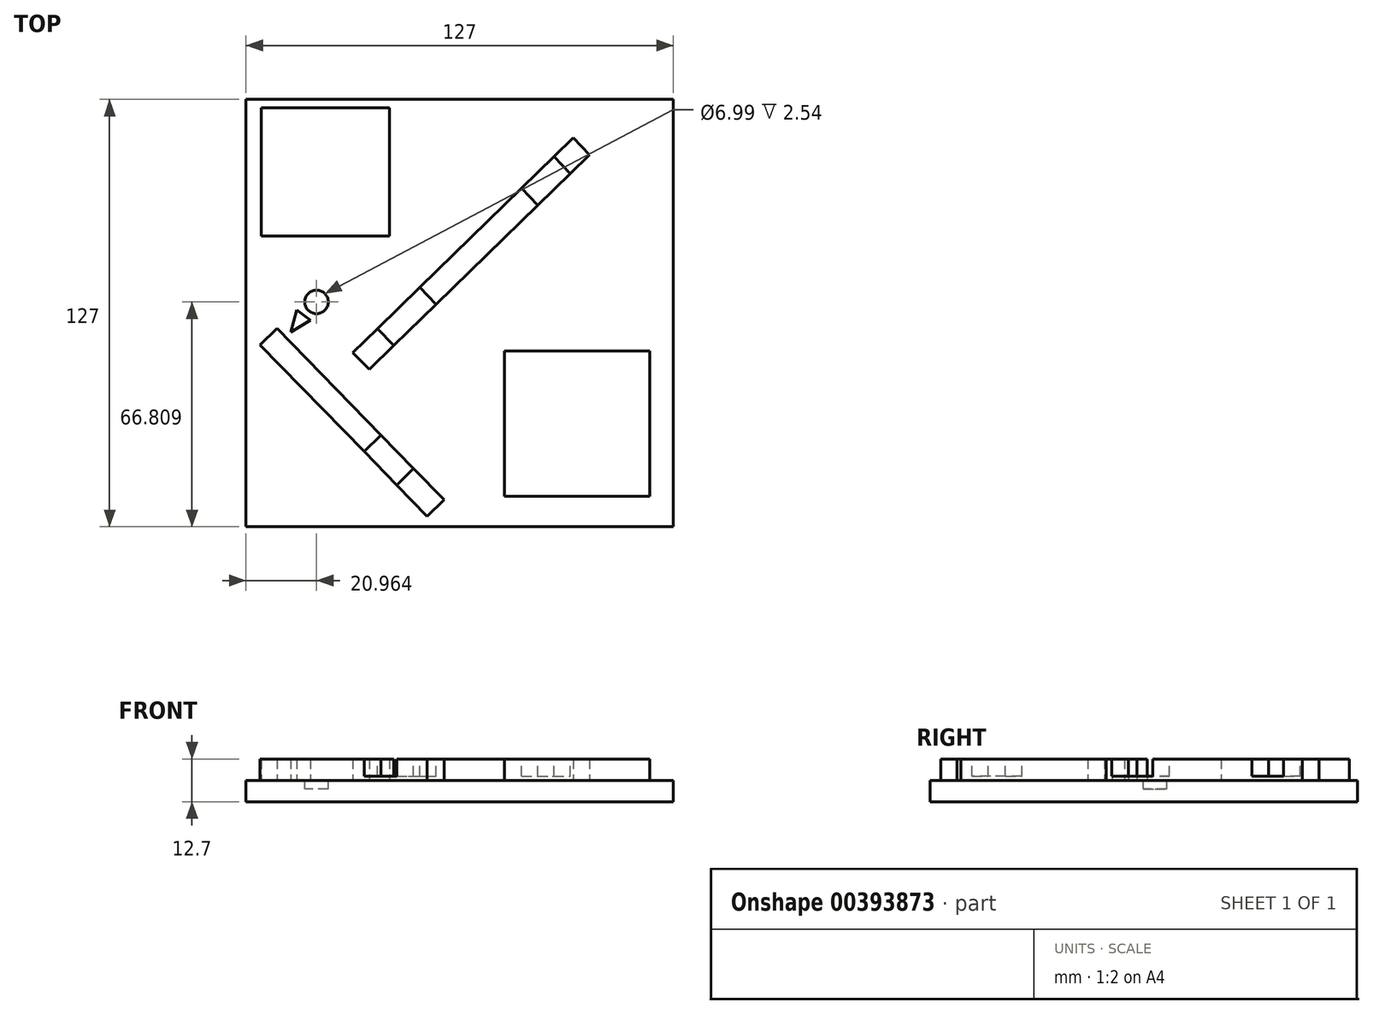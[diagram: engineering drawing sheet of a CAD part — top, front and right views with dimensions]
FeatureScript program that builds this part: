
annotation { "Feature Type Name" : "Feature", "Feature Type Description" : "" }
export const myFeature = defineFeature(function(context is Context, id is Id, definition is map)
    precondition{}
    {
        {
            var Q0;
            Q0=qCreatedBy(makeId("Top.planeOp"),FACE);
            var sketch = newSketch(context, id + "F0", { "sketchPlane" : qUnion([Q0])});
            skLineSegment(sketch, "E0.bottom", {"start": v(-62.96, 50.49) * mm, "end": v(64.04, 50.49) * mm});
            skLineSegment(sketch, "E0.top", {"start": v(-62.96, -76.51) * mm, "end": v(64.04, -76.51) * mm});
            skLineSegment(sketch, "E0.left", {"start": v(-62.96, 50.49) * mm, "end": v(-62.96, -76.51) * mm});
            skLineSegment(sketch, "E0.right", {"start": v(64.04, 50.49) * mm, "end": v(64.04, -76.51) * mm});
            skSolve(sketch);
        }
        {
            var Q0;
            Q0 = qSketchRegion(id + "F0", true);
            extrude(context, id + "F1", {"entities" : qUnion([Q0]), "depth" : 6.35 * mm});
        }
        {
            var Q0;
            Q0=makeQuery(id+"F1.opExtrude","CAP_FACE",FACE,{"disambiguationData":[OSD([sQuery(id+"F0.wireOp",EDGE,"E0.bottom"),sQuery(id+"F0.wireOp",EDGE,"E0.top"),sQuery(id+"F0.wireOp",EDGE,"E0.left"),sQuery(id+"F0.wireOp",EDGE,"E0.right")])],"isStart":false});
            var sketch = newSketch(context, id + "F2", { "sketchPlane" : qUnion([Q0])});
            skLineSegment(sketch, "E1", {"start": v(-58.74, -22.46) * mm, "end": v(-9.12, -73.4) * mm});
            skLineSegment(sketch, "E2", {"start": v(-9.12, -73.4) * mm, "end": v(-4.12, -68.53) * mm});
            skLineSegment(sketch, "E3", {"start": v(-58.74, -22.46) * mm, "end": v(-53.74, -17.59) * mm});
            skLineSegment(sketch, "E4", {"start": v(-53.74, -17.59) * mm, "end": v(-4.12, -68.53) * mm});
            skSolve(sketch);
        }
        {
            var Q0;
            Q0 = qSketchRegion(id + "F2", true);
            extrude(context, id + "F3", {"entities" : qUnion([Q0]), "operationType" : NewBodyOperationType.ADD, "depth" : 6.35 * mm});
        }
        {
            var Q0;
            Q0=makeQuery(id+"F3.opExtrude","CAP_FACE",FACE,{"disambiguationData":[OSD([sQuery(id+"F2.wireOp",EDGE,"E1"),sQuery(id+"F2.wireOp",EDGE,"E2"),sQuery(id+"F2.wireOp",EDGE,"E3"),sQuery(id+"F2.wireOp",EDGE,"E4")])],"isStart":false});
            var sketch = newSketch(context, id + "F4", { "sketchPlane" : qUnion([Q0])});
            skLineSegment(sketch, "E5", {"start": v(-27.84, -54.18) * mm, "end": v(-22.84, -49.31) * mm});
            skLineSegment(sketch, "E6", {"start": v(-18.16, -64.12) * mm, "end": v(-13.16, -59.25) * mm});
            skSolve(sketch);
        }
        {
            var Q0;
            {var subQ0=sQuery(id+"F4.wireOp",EDGE,"E5");Q0=makeQuery(id+"F4.imprint","IMPRINT",FACE,{"disambiguationData":[TD([[makeQuery(id+"F4.imprint","IMPRINT",EDGE,{"derivedFrom":subQ0}),-1.0]])]});}
            extrude(context, id + "F5", {"entities" : qUnion([Q0]), "operationType" : NewBodyOperationType.REMOVE, "oppositeDirection" : true, "depth" : 5.08 * mm});
        }
        {
            var Q0;
            Q0=makeQuery(id+"F1.opExtrude","CAP_FACE",FACE,{"disambiguationData":[OSD([sQuery(id+"F0.wireOp",EDGE,"E0.bottom"),sQuery(id+"F0.wireOp",EDGE,"E0.top"),sQuery(id+"F0.wireOp",EDGE,"E0.left"),sQuery(id+"F0.wireOp",EDGE,"E0.right")])],"isStart":false});
            var sketch = newSketch(context, id + "F6", { "sketchPlane" : qUnion([Q0])});
            skLineSegment(sketch, "E7.bottom", {"start": v(13.87, -24.28) * mm, "end": v(57.05, -24.28) * mm});
            skLineSegment(sketch, "E7.top", {"start": v(13.87, -67.46) * mm, "end": v(57.05, -67.46) * mm});
            skLineSegment(sketch, "E7.left", {"start": v(13.87, -24.28) * mm, "end": v(13.87, -67.46) * mm});
            skLineSegment(sketch, "E7.right", {"start": v(57.05, -24.28) * mm, "end": v(57.05, -67.46) * mm});
            skSolve(sketch);
        }
        {
            var Q0;
            Q0 = qSketchRegion(id + "F6", true);
            extrude(context, id + "F7", {"entities" : qUnion([Q0]), "operationType" : NewBodyOperationType.ADD, "depth" : 6.35 * mm});
        }
        {
            var Q0;
            Q0=makeQuery(id+"F1.opExtrude","CAP_FACE",FACE,{"disambiguationData":[OSD([sQuery(id+"F0.wireOp",EDGE,"E0.bottom"),sQuery(id+"F0.wireOp",EDGE,"E0.top"),sQuery(id+"F0.wireOp",EDGE,"E0.left"),sQuery(id+"F0.wireOp",EDGE,"E0.right")])],"isStart":false});
            var sketch = newSketch(context, id + "F8", { "sketchPlane" : qUnion([Q0])});
            skLineSegment(sketch, "E8", {"start": v(-31.22, -24.76) * mm, "end": v(-26.35, -29.77) * mm});
            skLineSegment(sketch, "E9", {"start": v(-31.22, -24.76) * mm, "end": v(34.29, 39.03) * mm});
            skLineSegment(sketch, "E10", {"start": v(34.29, 39.03) * mm, "end": v(39.16, 34.03) * mm});
            skLineSegment(sketch, "E11", {"start": v(-26.35, -29.77) * mm, "end": v(39.16, 34.03) * mm});
            skSolve(sketch);
        }
        {
            var Q0;
            Q0 = qSketchRegion(id + "F8", true);
            extrude(context, id + "F9", {"entities" : qUnion([Q0]), "operationType" : NewBodyOperationType.ADD, "depth" : 6.35 * mm});
        }
        {
            var Q0;
            Q0=makeQuery(id+"F9.opExtrude","CAP_FACE",FACE,{"disambiguationData":[OSD([sQuery(id+"F8.wireOp",EDGE,"E8"),sQuery(id+"F8.wireOp",EDGE,"E9"),sQuery(id+"F8.wireOp",EDGE,"E10"),sQuery(id+"F8.wireOp",EDGE,"E11")])],"isStart":false});
            var sketch = newSketch(context, id + "F10", { "sketchPlane" : qUnion([Q0])});
            skLineSegment(sketch, "E12", {"start": v(-23.88, -17.62) * mm, "end": v(-19, -22.62) * mm});
            skLineSegment(sketch, "E13", {"start": v(-11.34, -5.4) * mm, "end": v(-6.47, -10.41) * mm});
            skLineSegment(sketch, "E14", {"start": v(28.56, 33.46) * mm, "end": v(33.43, 28.45) * mm});
            skLineSegment(sketch, "E15", {"start": v(18.92, 24.07) * mm, "end": v(23.8, 19.07) * mm});
            skSolve(sketch);
        }
        {
            var Q0;
            {var subQ0=sQuery(id+"F10.wireOp",EDGE,"E12");Q0=makeQuery(id+"F10.imprint","IMPRINT",FACE,{"disambiguationData":[TD([[makeQuery(id+"F10.imprint","IMPRINT",EDGE,{"derivedFrom":subQ0}),1.0]])]});}
            var Q1;
            {var subQ0=sQuery(id+"F10.wireOp",EDGE,"E14");Q1=makeQuery(id+"F10.imprint","IMPRINT",FACE,{"disambiguationData":[TD([[makeQuery(id+"F10.imprint","IMPRINT",EDGE,{"derivedFrom":subQ0}),-1.0]])]});}
            extrude(context, id + "F11", {"entities" : qUnion([Q0, Q1]), "operationType" : NewBodyOperationType.REMOVE, "oppositeDirection" : true, "depth" : 5.08 * mm});
        }
        {
            var Q0;
            Q0=makeQuery(id+"F1.opExtrude","CAP_FACE",FACE,{"disambiguationData":[OSD([sQuery(id+"F0.wireOp",EDGE,"E0.bottom"),sQuery(id+"F0.wireOp",EDGE,"E0.top"),sQuery(id+"F0.wireOp",EDGE,"E0.left"),sQuery(id+"F0.wireOp",EDGE,"E0.right")])],"isStart":false});
            var sketch = newSketch(context, id + "F12", { "sketchPlane" : qUnion([Q0])});
            skLineSegment(sketch, "E16.bottom", {"start": v(-58.46, 47.95) * mm, "end": v(-20.36, 47.95) * mm});
            skLineSegment(sketch, "E16.top", {"start": v(-58.46, 9.85) * mm, "end": v(-20.36, 9.85) * mm});
            skLineSegment(sketch, "E16.left", {"start": v(-58.46, 47.95) * mm, "end": v(-58.46, 9.85) * mm});
            skLineSegment(sketch, "E16.right", {"start": v(-20.36, 47.95) * mm, "end": v(-20.36, 9.85) * mm});
            skSolve(sketch);
        }
        {
            var Q0;
            Q0 = qSketchRegion(id + "F12", true);
            extrude(context, id + "F13", {"entities" : qUnion([Q0]), "operationType" : NewBodyOperationType.ADD, "depth" : 6.35 * mm});
        }
        {
            var Q0;
            Q0=makeQuery(id+"F1.opExtrude","CAP_FACE",FACE,{"disambiguationData":[OSD([sQuery(id+"F0.wireOp",EDGE,"E0.bottom"),sQuery(id+"F0.wireOp",EDGE,"E0.top"),sQuery(id+"F0.wireOp",EDGE,"E0.left"),sQuery(id+"F0.wireOp",EDGE,"E0.right")])],"isStart":false});
            var sketch = newSketch(context, id + "F14", { "sketchPlane" : qUnion([Q0])});
            skCircle(sketch, "E17", {"center": v(-42, -9.7) * mm, "radius": 3.5 * mm});
            skSolve(sketch);
        }
        {
            var Q0;
            Q0 = qSketchRegion(id + "F14", true);
            extrude(context, id + "F15", {"entities" : qUnion([Q0]), "operationType" : NewBodyOperationType.REMOVE, "oppositeDirection" : true, "depth" : 2.54 * mm});
        }
        {
            var Q0;
            Q0=makeQuery(id+"F1.opExtrude","CAP_FACE",FACE,{"disambiguationData":[OSD([sQuery(id+"F0.wireOp",EDGE,"E0.bottom"),sQuery(id+"F0.wireOp",EDGE,"E0.top"),sQuery(id+"F0.wireOp",EDGE,"E0.left"),sQuery(id+"F0.wireOp",EDGE,"E0.right")])],"isStart":false});
            var sketch = newSketch(context, id + "F16", { "sketchPlane" : qUnion([Q0])});
            skLineSegment(sketch, "E18", {"start": v(-47.91, -12.1) * mm, "end": v(-49.66, -18.74) * mm});
            skLineSegment(sketch, "E19", {"start": v(-49.66, -18.74) * mm, "end": v(-43.83, -15.13) * mm});
            skLineSegment(sketch, "E20", {"start": v(-43.83, -15.13) * mm, "end": v(-47.91, -12.1) * mm});
            skSolve(sketch);
        }
        {
            var Q0;
            Q0 = qSketchRegion(id + "F16", true);
            extrude(context, id + "F17", {"entities" : qUnion([Q0]), "operationType" : NewBodyOperationType.ADD, "depth" : 6.35 * mm});
        }
    });
